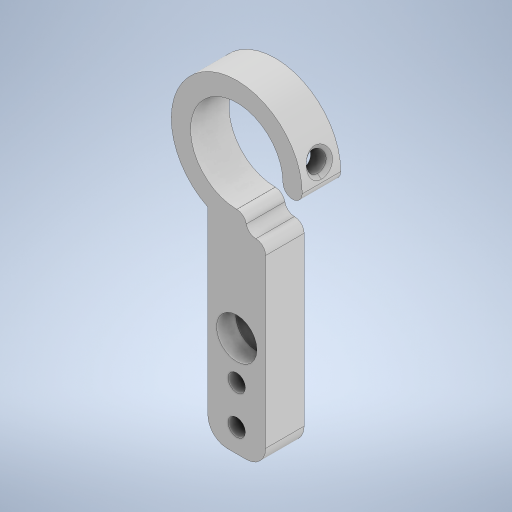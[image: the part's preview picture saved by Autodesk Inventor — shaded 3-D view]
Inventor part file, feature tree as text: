
AUTODESK INVENTOR PART (.ipt)
format: ipt  version: 2023 (Build 270158000, 158)  size: 332,800 bytes
history: native  units: mm
features: sketch x5, extrude x4, fillet x2, other x1, revolve x1, chamfer x1
ambient origin geometry x8: Origin, YZ Plane, XZ Plane, XY Plane, X Axis, Y Axis, Z Axis, Center Point
bodies: Body1 (feature_tree)
feature tree (14):
  other  "솔리드1"
  extrude  "돌출1"  Depth=15.0mm
  fillet  "모깎기1"  Radius=55.0mm
  revolve  "회전1"
  chamfer  "모따기1"  Distance=24.0mm
  extrude  "돌출2"  Depth=34.0mm
  fillet  "모깎기2"  Radius=10.0mm
  extrude  "돌출4"  Depth=2.5mm
  extrude  "돌출5"  Depth=1.745329mm
  sketch  "스케치1"
  sketch  "스케치2"
  sketch  "스케치3"
  sketch  "스케치5"
  sketch  "스케치6"
